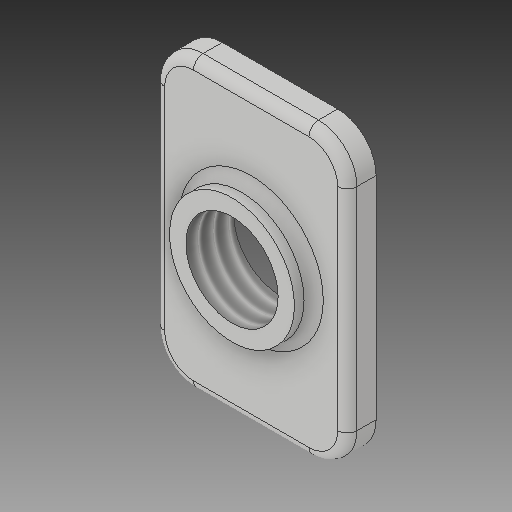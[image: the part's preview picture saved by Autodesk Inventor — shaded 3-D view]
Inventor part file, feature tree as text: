
AUTODESK INVENTOR PART (.ipt)
format: ipt  version: 2018 (Build 220112000, 112)  size: 165,376 bytes
history: native  units: mm
features: other x3, sketch x2
ambient origin geometry x8: Origin, YZ Plane, XZ Plane, XY Plane, X Axis, Y Axis, Z Axis, Center Point
bodies: Solid1 (feature_tree)
feature tree (5):
  other  "M5 Tee Nut_MIR.ipt"
  other  "Solid1::M5 Tee Nut_MIR.ipt"
  other  "TaggingFeature1"
  sketch  "Sketch1"  dims[d0=10.0mm]
  sketch  "Sketch2"
